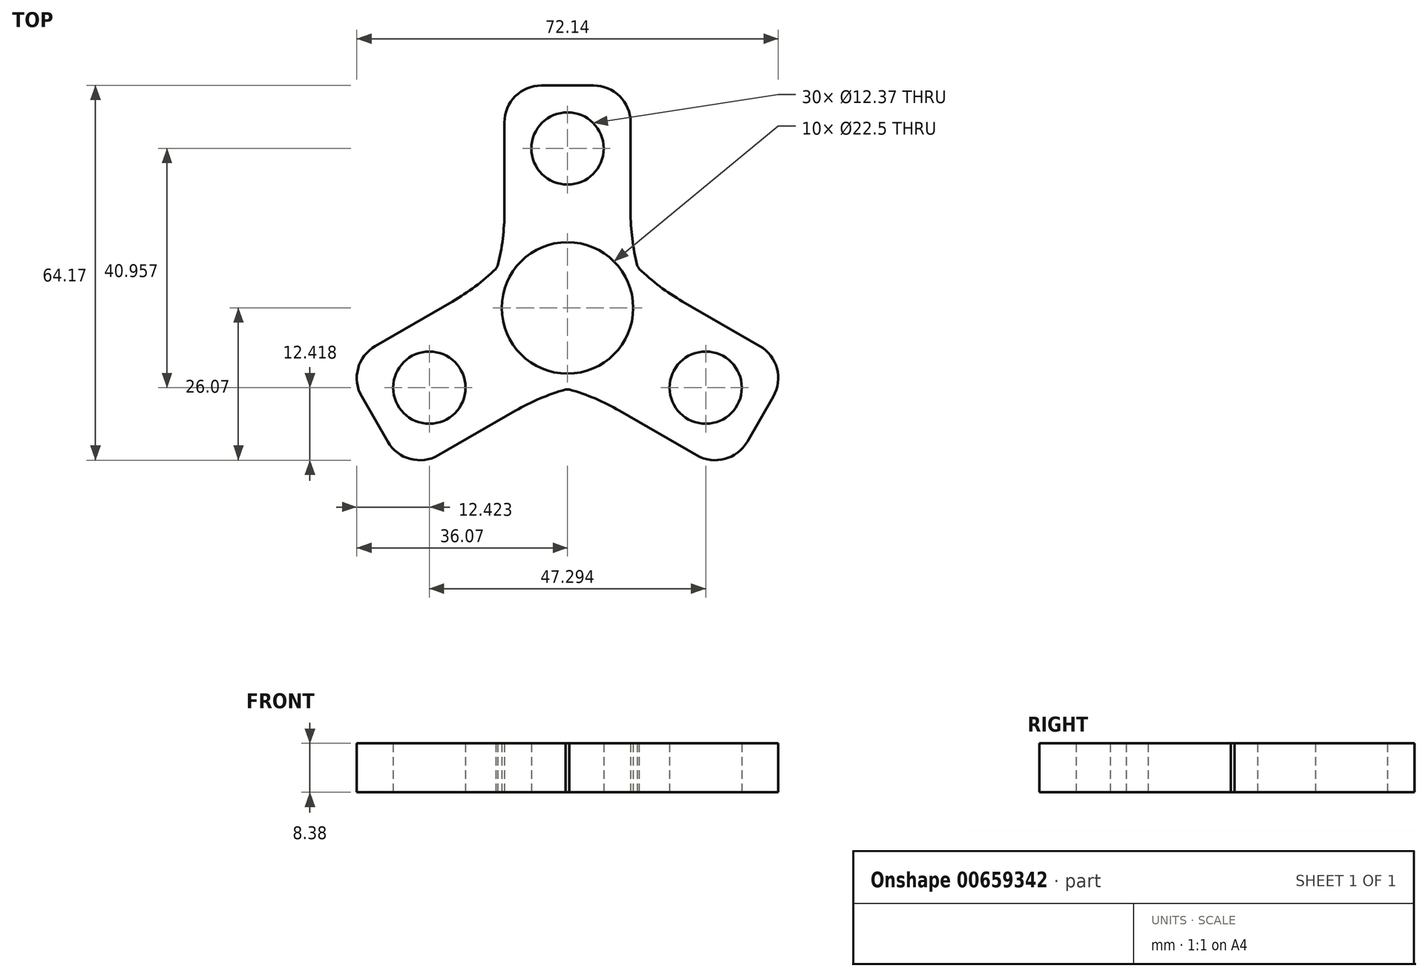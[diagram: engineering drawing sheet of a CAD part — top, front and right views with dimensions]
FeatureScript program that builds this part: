
annotation { "Feature Type Name" : "Feature", "Feature Type Description" : "" }
export const myFeature = defineFeature(function(context is Context, id is Id, definition is map)
    precondition{}
    {
        {
            var Q0;
            Q0=qCreatedBy(makeId("Top.planeOp"),FACE);
            var sketch = newSketch(context, id + "F0", { "sketchPlane" : qUnion([Q0])});
            skCircle(sketch, "E0", {"center": v(0, 0) * mm, "radius": 11.25 * mm});
            skArc(sketch, "E1", {"start": v(-11.93, 7.27) * mm, "mid": v(-12.1, 6.98) * mm, "end": v(-12.26, 6.7) * mm});
            skCircle(sketch, "E2.cCircle", {"center": v(0, 27.3) * mm, "radius": 10.8 * mm, "construction": true});
            skLineSegment(sketch, "E2.0", {"start": v(-10.8, 16.51) * mm, "end": v(-10.8, 31.75) * mm});
            skLineSegment(sketch, "E2.1", {"start": v(-4.45, 38.1) * mm, "end": v(4.44, 38.1) * mm});
            skLineSegment(sketch, "E2.2", {"start": v(10.8, 31.75) * mm, "end": v(10.8, 16.51) * mm});
            skPoint(sketch, "E2.0.midPoint", {"position": v(-10.8, 27.3) * mm});
            skArc(sketch, "E3", {"start": v(10.8, 16.5) * mm, "mid": v(11.08, 11.86) * mm, "end": v(11.93, 7.27) * mm});
            skArc(sketch, "E4", {"start": v(-11.93, 7.27) * mm, "mid": v(-11.08, 11.86) * mm, "end": v(-10.8, 16.51) * mm});
            skPoint(sketch, "E5.visualSharp", {"position": v(10.8, 38.1) * mm});
            skArc(sketch, "E5.filletArc", {"start": v(10.8, 31.75) * mm, "mid": v(8.94, 36.24) * mm, "end": v(4.44, 38.1) * mm});
            skPoint(sketch, "E6.visualSharp", {"position": v(-10.8, 38.1) * mm});
            skArc(sketch, "E6.filletArc", {"start": v(-4.45, 38.1) * mm, "mid": v(-8.94, 36.24) * mm, "end": v(-10.8, 31.75) * mm});
            skCircle(sketch, "E7", {"center": v(0, 27.3) * mm, "radius": 6.19 * mm});
            skLineSegment(sketch, "E8.1.0", {"start": v(-32.9, -6.53) * mm, "end": v(-19.7, 1.1) * mm});
            skArc(sketch, "E8.1.1", {"start": v(-32.9, -6.53) * mm, "mid": v(-35.85, -10.38) * mm, "end": v(-35.22, -15.2) * mm});
            skLineSegment(sketch, "E8.1.2", {"start": v(-30.77, -22.9) * mm, "end": v(-35.22, -15.2) * mm});
            skArc(sketch, "E8.1.3", {"start": v(-30.77, -22.9) * mm, "mid": v(-26.92, -25.86) * mm, "end": v(-22.1, -25.22) * mm});
            skLineSegment(sketch, "E8.1.4", {"start": v(-8.9, -17.6) * mm, "end": v(-22.1, -25.22) * mm});
            skArc(sketch, "E8.1.5", {"start": v(-0.33, -13.97) * mm, "mid": v(-4.73, -15.52) * mm, "end": v(-8.9, -17.6) * mm});
            skArc(sketch, "E8.1.6", {"start": v(-19.7, 1.1) * mm, "mid": v(-15.8, 3.67) * mm, "end": v(-12.26, 6.7) * mm});
            skCircle(sketch, "E8.1.7", {"center": v(-23.65, -13.65) * mm, "radius": 6.19 * mm});
            skLineSegment(sketch, "E8.2.0", {"start": v(22.1, -25.22) * mm, "end": v(8.9, -17.6) * mm});
            skArc(sketch, "E8.2.1", {"start": v(22.1, -25.22) * mm, "mid": v(26.92, -25.86) * mm, "end": v(30.77, -22.9) * mm});
            skLineSegment(sketch, "E8.2.2", {"start": v(35.22, -15.2) * mm, "end": v(30.77, -22.9) * mm});
            skArc(sketch, "E8.2.3", {"start": v(35.22, -15.2) * mm, "mid": v(35.85, -10.38) * mm, "end": v(32.9, -6.53) * mm});
            skLineSegment(sketch, "E8.2.4", {"start": v(19.7, 1.1) * mm, "end": v(32.9, -6.53) * mm});
            skArc(sketch, "E8.2.5", {"start": v(12.26, 6.7) * mm, "mid": v(15.8, 3.67) * mm, "end": v(19.7, 1.1) * mm});
            skArc(sketch, "E8.2.6", {"start": v(8.9, -17.6) * mm, "mid": v(4.73, -15.52) * mm, "end": v(0.33, -13.97) * mm});
            skCircle(sketch, "E8.2.7", {"center": v(23.65, -13.65) * mm, "radius": 6.19 * mm});
            skArc(sketch, "E9.trimOffspring", {"start": v(12.26, 6.7) * mm, "mid": v(12.1, 6.98) * mm, "end": v(11.93, 7.27) * mm});
            skArc(sketch, "E10.trimOffspring", {"start": v(-0.33, -13.97) * mm, "mid": v(0, -13.97) * mm, "end": v(0.33, -13.97) * mm});
            skSolve(sketch);
        }
        {
            var Q0;
            Q0=makeQuery(id+"F0.imprint","IMPRINT",FACE,{"disambiguationData":[TD([[makeQuery(id+"F0.imprint","IMPRINT",EDGE,{"derivedFrom":sQuery(id+"F0.wireOp",EDGE,"E0")}),-1.0]])]});
            extrude(context, id + "F1", {"entities" : qUnion([Q0]), "depth" : 8.38 * mm, "offsetDistance" : 25.4 * mm});
        }
    });
